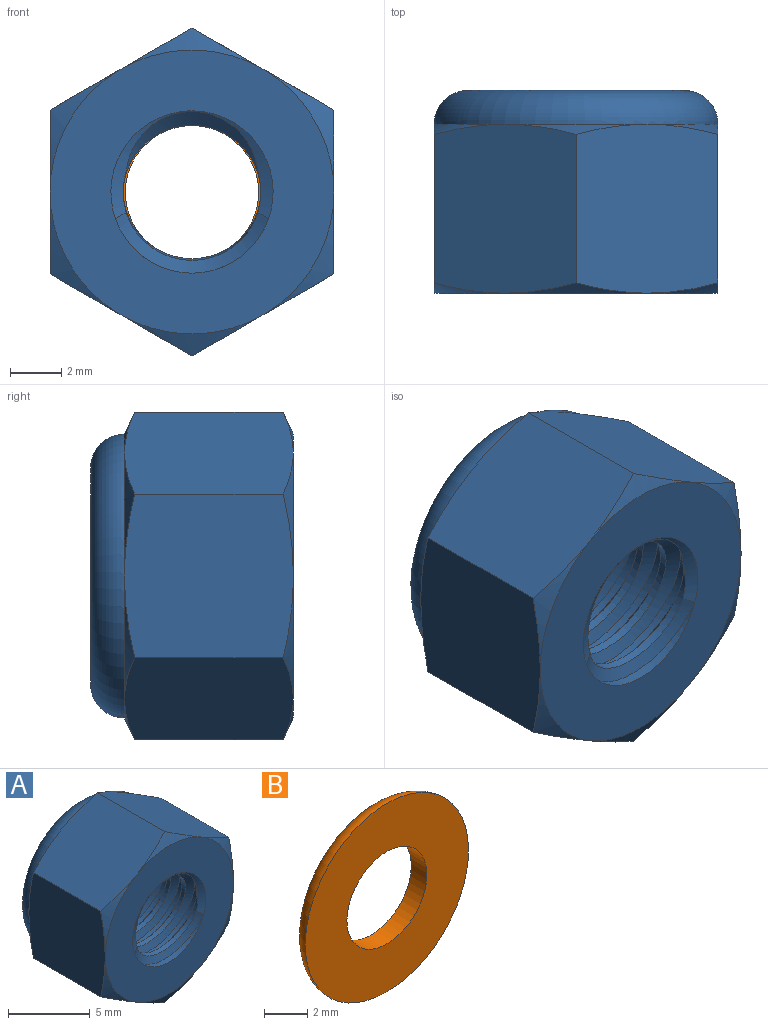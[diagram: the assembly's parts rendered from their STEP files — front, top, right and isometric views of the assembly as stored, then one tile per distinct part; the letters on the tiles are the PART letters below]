
ASSEMBLY  parts=2 mates=1
PART A: 51 faces, bbox 13.3x8.6x13.3 mm
  f0: torus R=4.23mm, axis (0,-1,0), area 57.5mm2, adj f49,f50
  f1: cylinder r=3.42mm len=6.84mm, axis (0,-1,0), area 3.3mm2, adj f27,f50
  f2: torus R=4.23mm, axis (0,-1,0), area 66.3mm2, adj f3,f27,f38,f39,f40,f41,f42
  f3: cone r=5.56mm half-angle=65deg, axis (0,-1,0), area 2.9mm2, adj f2,f47,f48
  f4: cone r=6.42mm half-angle=65deg, axis (0,1,0), area 2.9mm2, adj f28,f44,f45
  f5: cylinder r=3.17mm len=6mm, axis (0,-1,0), area 1.7mm2, adj f25,f28
  f6: cone r=2.69mm half-angle=60deg, axis (0,-0.98,-0.2), area 12mm2, adj f7,f24
  f7: cylinder r=2.69mm len=5.39mm, axis (0,0.98,0.2), area 5.4mm2, adj f6,f8
  f8: cone r=3.38mm half-angle=60deg, axis (0,0.98,0.2), area 12mm2, adj f7,f23
  f9: cone r=2.69mm half-angle=60deg, axis (0,-0.98,-0.2), area 12mm2, adj f10,f23
  f10: cylinder r=2.69mm len=5.39mm, axis (0,0.98,0.2), area 5.4mm2, adj f9,f11
  f11: cone r=3.38mm half-angle=60deg, axis (0,0.98,0.2), area 12mm2, adj f10,f22
  f12: cone r=2.69mm half-angle=60deg, axis (0,-0.98,-0.2), area 12mm2, adj f13,f22
  f13: cylinder r=2.69mm len=5.39mm, axis (0,0.98,0.2), area 5.4mm2, adj f12,f14
  f14: cone r=3.38mm half-angle=60deg, axis (0,0.98,0.2), area 12mm2, adj f13,f21
  f15: cone r=2.69mm half-angle=60deg, axis (0,-0.98,-0.2), area 12mm2, adj f16,f21
  f16: cylinder r=2.69mm len=5.39mm, axis (0,0.98,0.2), area 5.4mm2, adj f15,f17
  f17: cone r=3.38mm half-angle=60deg, axis (0,0.98,0.2), area 12mm2, adj f16,f20
  f18: cylinder r=2.69mm len=5.39mm, axis (0,0.98,0.2), area 2.8mm2, adj f19,f32,f49
  f19: cone r=3.38mm half-angle=60deg, axis (0,0.98,0.2), area 3.5mm2, adj f18,f31,f49
  f20: cylinder r=3.17mm len=6.35mm, axis (0,-1,0), area 6.2mm2, adj f17,f32,f49
  f21: cylinder r=3.17mm len=6.35mm, axis (0,-1,0), area 6.8mm2, adj f14,f15
  f22: cylinder r=3.17mm len=6.35mm, axis (0,-1,0), area 6.8mm2, adj f11,f12
  f23: cylinder r=3.17mm len=6.35mm, axis (0,-1,0), area 6.8mm2, adj f8,f9
  f24: cylinder r=3.17mm len=6.35mm, axis (0,-1,0), area 6.8mm2, adj f6,f26
  f25: cone r=2.69mm half-angle=60deg, axis (0,-0.98,-0.2), area 3.9mm2, adj f5,f29,f30
  f26: cone r=3.38mm half-angle=60deg, axis (0,0.98,0.2), area 8.8mm2, adj f24,f29,f30
  f27: plane 8.47x8.47mm, normal (0,1,0), area 19.5mm2, adj f1,f2
  f28: plane 11.11x11.11mm, normal (0,-1,0), area 65.3mm2, adj f4,f5,f29,f33,f34,f35,f36,f37
  f29: cone r=3.17mm half-angle=65deg, axis (0,-1,0), area 4.1mm2, adj f25,f26,f28,f30
  f30: cylinder r=2.69mm len=5.39mm, axis (0,0.98,0.2), area 2.7mm2, adj f25,f26,f29
  f31: cylinder r=3.17mm len=5.02mm, axis (0,-1,0), area 0.7mm2, adj f19,f49
  f32: cone r=2.69mm half-angle=60deg, axis (0,-0.98,-0.2), area 8.4mm2, adj f18,f20,f49
  f33: cone r=6.42mm half-angle=65deg, axis (0,1,0), area 2.9mm2, adj f28,f47,f48
  f34: cone r=6.42mm half-angle=65deg, axis (0,1,0), area 2.9mm2, adj f28,f43,f48
  f35: cone r=6.42mm half-angle=65deg, axis (0,1,0), area 2.9mm2, adj f28,f43,f44
  f36: cone r=6.42mm half-angle=65deg, axis (0,1,0), area 2.9mm2, adj f28,f45,f46
  f37: cone r=6.42mm half-angle=65deg, axis (0,1,0), area 2.9mm2, adj f28,f46,f47
  f38: cone r=5.56mm half-angle=65deg, axis (0,-1,0), area 2.9mm2, adj f2,f45,f46
  f39: cone r=5.56mm half-angle=65deg, axis (0,-1,0), area 2.9mm2, adj f2,f46,f47
  f40: cone r=5.56mm half-angle=65deg, axis (0,-1,0), area 2.9mm2, adj f2,f44,f45
  f41: cone r=5.56mm half-angle=65deg, axis (0,-1,0), area 2.9mm2, adj f2,f43,f48
  f42: cone r=5.56mm half-angle=65deg, axis (0,-1,0), area 2.9mm2, adj f2,f43,f44
  f43: plane 7.12x6.92mm, normal (1,0,0), area 40.7mm2, adj f34,f35,f41,f42,f44,f48
  f44: plane 7.12x6.06mm, normal (0.5,0,0.87), area 40.7mm2, adj f4,f35,f40,f42,f43,f45
  f45: plane 7.12x6.06mm, normal (-0.5,0,0.87), area 40.7mm2, adj f4,f36,f38,f40,f44,f46
  f46: plane 7.12x6.92mm, normal (-1,0,0), area 40.7mm2, adj f36,f37,f38,f39,f45,f47
  f47: plane 7.12x6.06mm, normal (-0.5,0,-0.87), area 40.7mm2, adj f3,f33,f37,f39,f46,f48
  f48: plane 7.12x6.06mm, normal (0.5,0,-0.87), area 40.7mm2, adj f3,f33,f34,f41,f43,f47
  f49: plane 10.86x10.86mm, normal (0,1,0), area 63.1mm2, adj f0,f18,f19,f20,f31,f32
  f50: plane 8.47x8.47mm, normal (0,-1,0), area 19.5mm2, adj f0,f1
PART B: 4 faces, bbox 11.5x1.1x11.5 mm
  f0: torus R=4.23mm, axis (0,-1,0), area 50.7mm2, adj f2,f3
  f1: cylinder r=2.61mm len=5.22mm, axis (0,-1,0), area 16.7mm2, adj f2,f3
  f2: plane 10.65x10.65mm, normal (0,-1,0), area 67.7mm2, adj f0,f1
  f3: plane 8.47x8.47mm, normal (0,1,0), area 34.9mm2, adj f0,f1
PLACE A at identity
PLACE B t=(0,-0.08,-0.01)mm
MATE fastened B.f1 <-> A.f49  axis (0,-1,0) through (0,6.61,-0.01)mm
